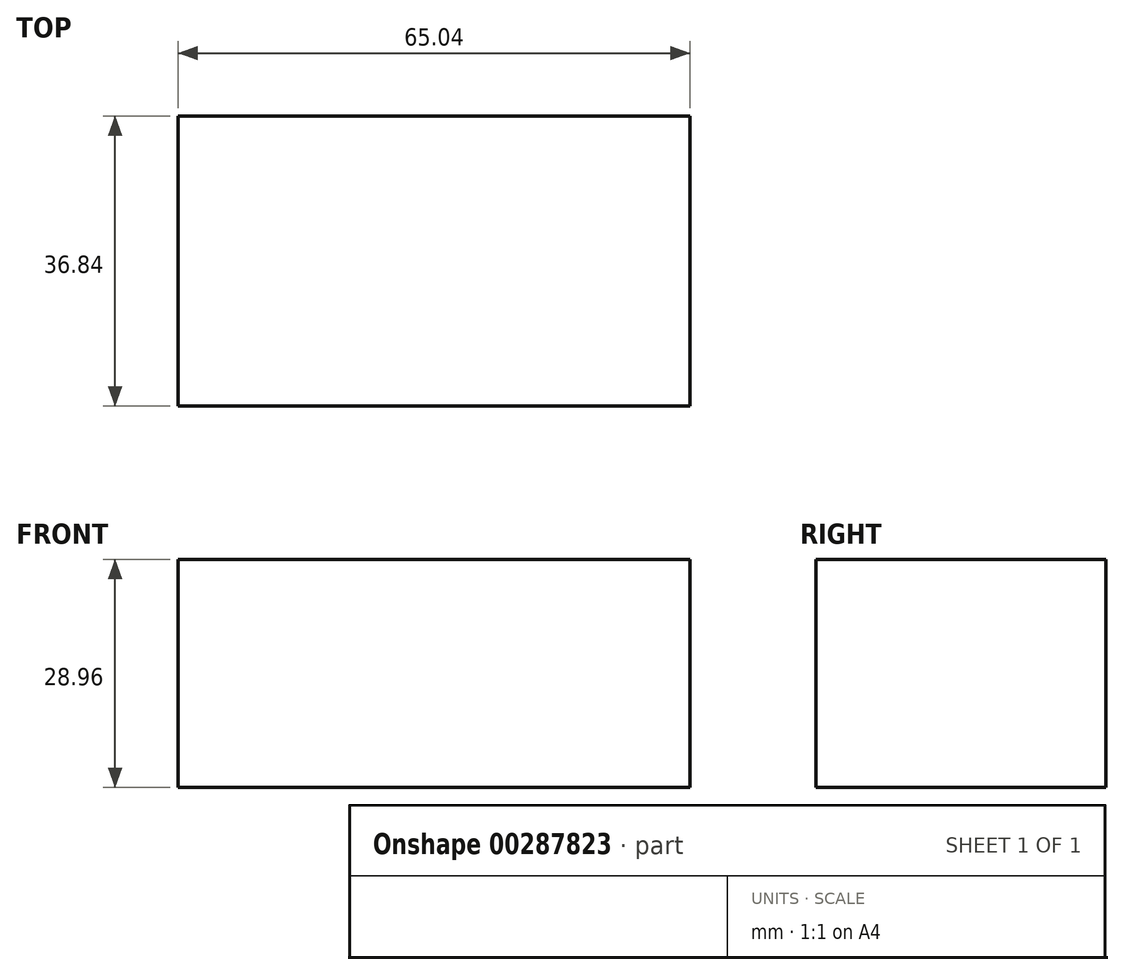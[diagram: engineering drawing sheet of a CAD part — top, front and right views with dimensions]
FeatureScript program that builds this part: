
annotation { "Feature Type Name" : "Feature", "Feature Type Description" : "" }
export const myFeature = defineFeature(function(context is Context, id is Id, definition is map)
    precondition{}
    {
        {
            var Q0;
            Q0=qCreatedBy(makeId("Front.planeOp"),FACE);
            var sketch = newSketch(context, id + "F0", { "sketchPlane" : qUnion([Q0])});
            skLineSegment(sketch, "E0.bottom", {"start": v(-28.78, 27.34) * mm, "end": v(32.8, 27.34) * mm});
            skLineSegment(sketch, "E0.top", {"start": v(-28.78, -12.95) * mm, "end": v(32.8, -12.95) * mm});
            skLineSegment(sketch, "E0.left", {"start": v(-28.78, 27.34) * mm, "end": v(-28.78, -12.95) * mm});
            skLineSegment(sketch, "E0.right", {"start": v(32.8, 27.34) * mm, "end": v(32.8, -12.95) * mm});
            skSolve(sketch);
        }
        {
            var Q0;
            Q0=qCreatedBy(makeId("Top.planeOp"),FACE);
            var sketch = newSketch(context, id + "F1", { "sketchPlane" : qUnion([Q0])});
            skLineSegment(sketch, "E1.bottom", {"start": v(-28.5, 0) * mm, "end": v(36.55, 0) * mm});
            skLineSegment(sketch, "E1.top", {"start": v(-28.5, 36.84) * mm, "end": v(36.55, 36.84) * mm});
            skLineSegment(sketch, "E1.left", {"start": v(-28.5, 0) * mm, "end": v(-28.5, 36.84) * mm});
            skLineSegment(sketch, "E1.right", {"start": v(36.55, 0) * mm, "end": v(36.55, 36.84) * mm});
            skLineSegment(sketch, "E2.0.1", {"start": v(-28.78, 0) * mm, "end": v(32.8, 0) * mm});
            skLineSegment(sketch, "E2.0.3", {"start": v(32.8, 0) * mm, "end": v(-28.78, 0) * mm});
            skSolve(sketch);
        }
        {
            var Q0;
            Q0 = qSketchRegion(id + "F1", true);
            extrude(context, id + "F2", {"entities" : qUnion([Q0]), "depth" : 28.96 * mm});
        }
    });
